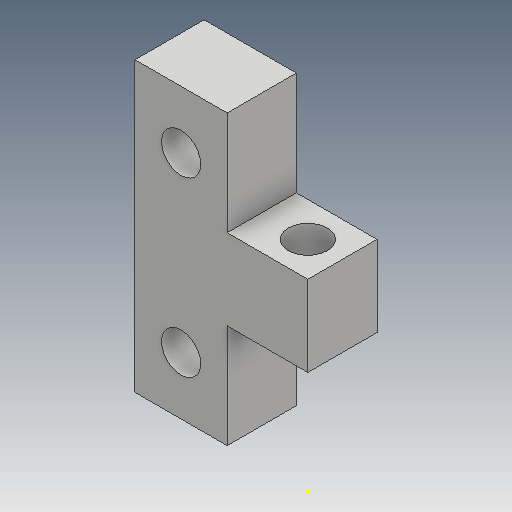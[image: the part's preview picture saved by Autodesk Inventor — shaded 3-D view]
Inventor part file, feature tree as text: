
AUTODESK INVENTOR PART (.ipt)
format: ipt  version: 2018 (Build 220112000, 112)  size: 134,656 bytes
history: native  units: mm
features: sketch x5, extrude x4
ambient origin geometry x8: Origin, YZ Plane, XZ Plane, XY Plane, X Axis, Y Axis, Z Axis, Center Point
bodies: Volumenkörper1 (feature_tree)
feature tree (9):
  extrude  "Extrusion1"  Depth=15.0mm
  sketch  "Skizze3"  dims[d2=6.0mm d3=0.0mm d11=3.4mm]
  extrude  "Extrusion4"  Depth=6.0mm
  extrude  "Extrusion5"  Depth=5.0mm
  extrude  "Extrusion6"  Depth=4.0mm
  sketch  "Skizze1"  dims[d0=25.0mm d1=15.0mm]
  sketch  "Skizze6"  dims[d12=4.0mm d13=5.0mm]
  sketch  "Skizze7"  dims[d14=3.4mm d15=4.0mm]
  sketch  "Skizze8"  dims[d16=5.0mm d17=30.0mm d18=0.0mm d19=7.0mm d20=9.0mm d21=7.0mm d22=9.0mm d23=30.0mm d24=0.0mm d25=3.4mm d26=3.0mm d27=3.0mm d28=30.0mm d29=0.0mm]
